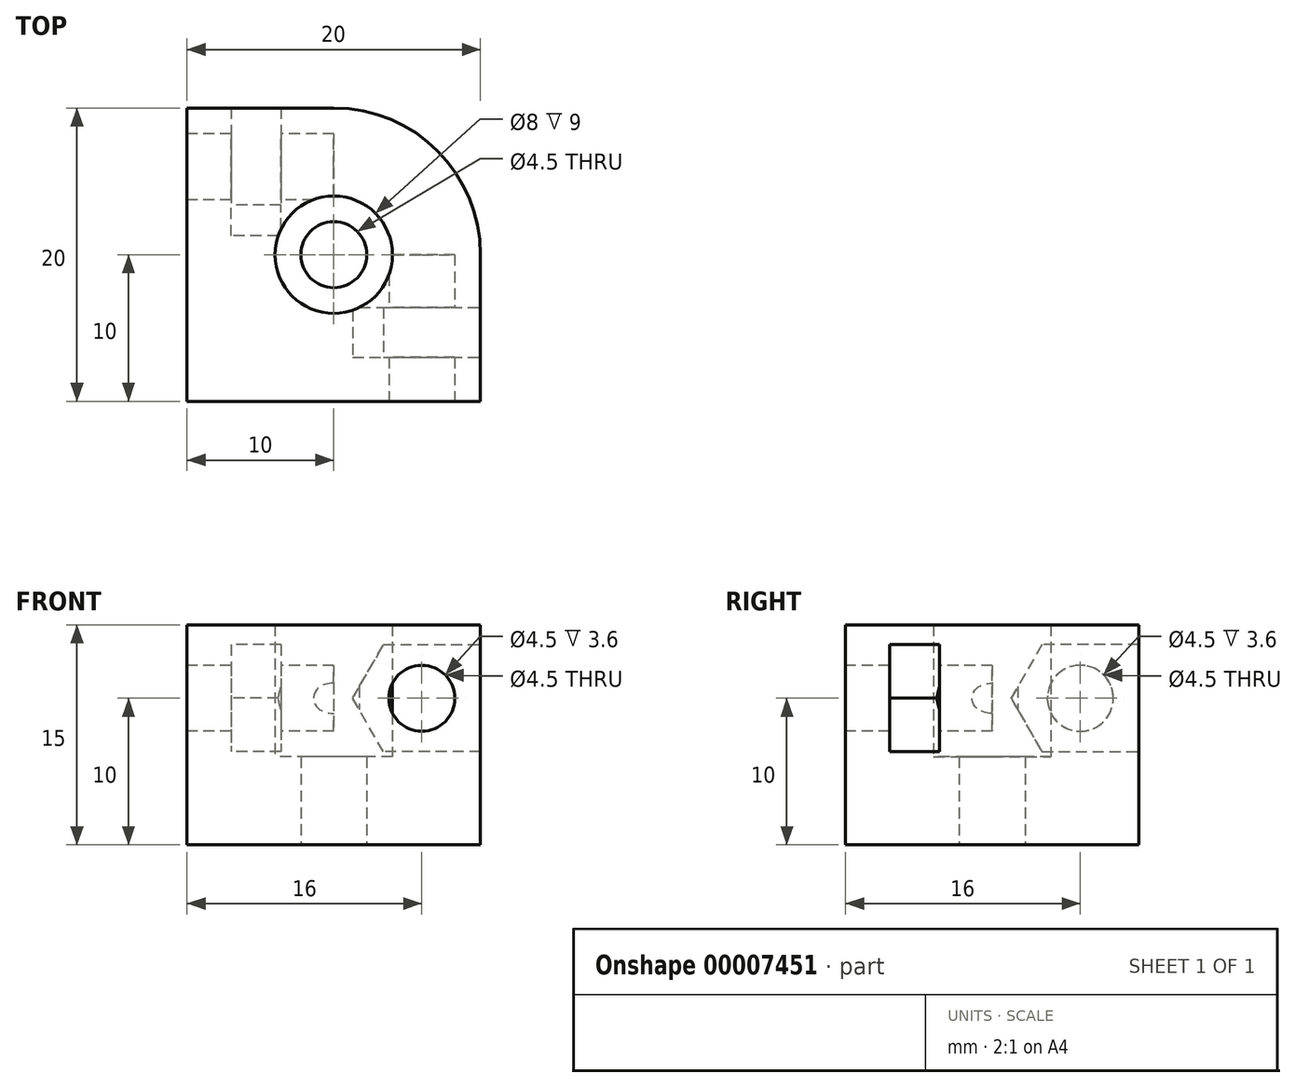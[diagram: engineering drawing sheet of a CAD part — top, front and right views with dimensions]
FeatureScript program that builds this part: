
annotation { "Feature Type Name" : "Feature", "Feature Type Description" : "" }
export const myFeature = defineFeature(function(context is Context, id is Id, definition is map)
    precondition{}
    {
        {
            var Q0;
            Q0=qCreatedBy(makeId("Top.planeOp"),FACE);
            var sketch = newSketch(context, id + "F0", { "sketchPlane" : qUnion([Q0])});
            skLineSegment(sketch, "E0", {"start": v(0, 0) * mm, "end": v(0, 20) * mm});
            skLineSegment(sketch, "E1", {"start": v(0, 20) * mm, "end": v(20, 20) * mm});
            skLineSegment(sketch, "E2", {"start": v(20, 20) * mm, "end": v(20, 0) * mm});
            skLineSegment(sketch, "E3", {"start": v(20, 0) * mm, "end": v(0, 0) * mm});
            skCircle(sketch, "E4", {"center": v(10, 10) * mm, "radius": 2.25 * mm});
            skCircle(sketch, "E5", {"center": v(10, 10) * mm, "radius": 4 * mm});
            skSolve(sketch);
        }
        {
            var Q0;
            Q0=makeQuery(id+"F0.imprint","IMPRINT",FACE,{"disambiguationData":[TD([[makeQuery(id+"F0.imprint","IMPRINT",EDGE,{"derivedFrom":sQuery(id+"F0.wireOp",EDGE,"E0")}),-1.0]])]});
            extrude(context, id + "F1", {"entities" : qUnion([Q0]), "depth" : 15 * mm});
        }
        {
            var Q0;
            Q0=makeQuery(id+"F0.imprint","IMPRINT",FACE,{"disambiguationData":[TD([[makeQuery(id+"F0.imprint","IMPRINT",EDGE,{"derivedFrom":sQuery(id+"F0.wireOp",EDGE,"E4")}),-1.0]])]});
            extrude(context, id + "F2", {"entities" : qUnion([Q0]), "operationType" : NewBodyOperationType.ADD, "depth" : 6 * mm});
        }
        {
            var Q0;
            Q0=makeQuery(id+"F1.opExtrude","SWEPT_FACE",FACE,{"disambiguationData":[OSD([sQuery(id+"F0.wireOp",EDGE,"E0")])]});
            var sketch = newSketch(context, id + "F3", { "sketchPlane" : qUnion([Q0])});
            skCircle(sketch, "E6", {"center": v(-16, 10) * mm, "radius": 2.25 * mm});
            skLineSegment(sketch, "E7.2", {"start": v(-13.4, 13.65) * mm, "end": v(-11.29, 10) * mm});
            skLineSegment(sketch, "E7.3", {"start": v(-11.29, 10) * mm, "end": v(-13.4, 6.35) * mm});
            skLineSegment(sketch, "E8", {"start": v(-20, 13.65) * mm, "end": v(-20, 6.35) * mm});
            skLineSegment(sketch, "E9", {"start": v(-20, 13.65) * mm, "end": v(-13.4, 13.65) * mm});
            skLineSegment(sketch, "E10", {"start": v(-13.4, 6.35) * mm, "end": v(-20, 6.35) * mm});
            skLineSegment(sketch, "E11", {"start": v(-16, 10) * mm, "end": v(-15.5, 10) * mm, "construction": true});
            skLineSegment(sketch, "E12", {"start": v(-15.5, 10) * mm, "end": v(-11.29, 10) * mm, "construction": true});
            skLineSegment(sketch, "E13", {"start": v(-12.34, 11.83) * mm, "end": v(-15.5, 10) * mm, "construction": true});
            skSolve(sketch);
        }
        {
            var Q0;
            Q0=makeQuery(id+"F3.imprint","IMPRINT",FACE,{"disambiguationData":[TD([[makeQuery(id+"F3.imprint","IMPRINT",EDGE,{"derivedFrom":sQuery(id+"F3.wireOp",EDGE,"E6")}),1.0]])]});
            extrude(context, id + "F4", {"entities" : qUnion([Q0]), "operationType" : NewBodyOperationType.REMOVE, "oppositeDirection" : true, "depth" : 10 * mm});
        }
        {
            var Q0;
            Q0 = qSketchRegion(id + "F3", true);
            extrude(context, id + "F5", {"entities" : qUnion([Q0]), "operationType" : NewBodyOperationType.REMOVE, "oppositeDirection" : true, "depth" : (3.4 + 3) * mm});
        }
        {
            var Q0;
            Q0=makeQuery(id+"F3.imprint","IMPRINT",FACE,{"disambiguationData":[TD([[makeQuery(id+"F3.imprint","IMPRINT",EDGE,{"derivedFrom":sQuery(id+"F3.wireOp",EDGE,"E6")}),-1.0]])]});
            extrude(context, id + "F6", {"entities" : qUnion([Q0]), "operationType" : NewBodyOperationType.ADD, "oppositeDirection" : true, "depth" : 3 * mm});
        }
        {
            var Q0;
            Q0=makeQuery(id+"F1.opExtrude","SWEPT_FACE",FACE,{"disambiguationData":[OSD([sQuery(id+"F0.wireOp",EDGE,"E3")])]});
            var sketch = newSketch(context, id + "F7", { "sketchPlane" : qUnion([Q0])});
            skCircle(sketch, "E14", {"center": v(16, 10) * mm, "radius": 2.25 * mm});
            skLineSegment(sketch, "E15.4", {"start": v(13.4, 6.35) * mm, "end": v(11.29, 10) * mm});
            skLineSegment(sketch, "E15.5", {"start": v(11.29, 10) * mm, "end": v(13.4, 13.65) * mm});
            skLineSegment(sketch, "E16", {"start": v(20, 13.65) * mm, "end": v(20, 6.35) * mm});
            skLineSegment(sketch, "E17", {"start": v(11.29, 10) * mm, "end": v(15.5, 10) * mm, "construction": true});
            skLineSegment(sketch, "E18", {"start": v(15.5, 10) * mm, "end": v(16, 10) * mm, "construction": true});
            skLineSegment(sketch, "E19", {"start": v(15.5, 10) * mm, "end": v(12.34, 11.83) * mm, "construction": true});
            skLineSegment(sketch, "E20", {"start": v(13.4, 13.65) * mm, "end": v(20, 13.65) * mm});
            skLineSegment(sketch, "E21", {"start": v(20, 6.35) * mm, "end": v(13.4, 6.35) * mm});
            skSolve(sketch);
        }
        {
            var Q0;
            Q0=makeQuery(id+"F7.imprint","IMPRINT",FACE,{"disambiguationData":[TD([[makeQuery(id+"F7.imprint","IMPRINT",EDGE,{"derivedFrom":sQuery(id+"F7.wireOp",EDGE,"E14")}),1.0]])]});
            extrude(context, id + "F8", {"entities" : qUnion([Q0]), "operationType" : NewBodyOperationType.REMOVE, "oppositeDirection" : true, "depth" : 10 * mm});
        }
        {
            var Q0;
            Q0=makeQuery(id+"F7.imprint","IMPRINT",FACE,{"disambiguationData":[TD([[makeQuery(id+"F7.imprint","IMPRINT",EDGE,{"derivedFrom":sQuery(id+"F7.wireOp",EDGE,"E14")}),-1.0]])]});
            extrude(context, id + "F9", {"entities" : qUnion([Q0]), "operationType" : NewBodyOperationType.REMOVE, "oppositeDirection" : true, "depth" : (3.4 + 3) * mm});
        }
        {
            var Q0;
            Q0=makeQuery(id+"F7.imprint","IMPRINT",FACE,{"disambiguationData":[TD([[makeQuery(id+"F7.imprint","IMPRINT",EDGE,{"derivedFrom":sQuery(id+"F7.wireOp",EDGE,"E14")}),-1.0]])]});
            extrude(context, id + "F10", {"entities" : qUnion([Q0]), "operationType" : NewBodyOperationType.ADD, "oppositeDirection" : true, "depth" : 3 * mm});
        }
        {
            var Q0;
            Q0=makeQuery(id+"F1.opExtrude","SWEPT_EDGE",EDGE,{"disambiguationData":[OSD([sQuery(id+"F0.wireOp",EDGE,"E1"),sQuery(id+"F0.wireOp",EDGE,"E2")])]});
            fillet(context, id + "F11", {"entities" : qUnion([Q0]), "radius" : 10 * mm, "tangentPropagation" : true, "allowEdgeOverflow" : false});
        }
    });
